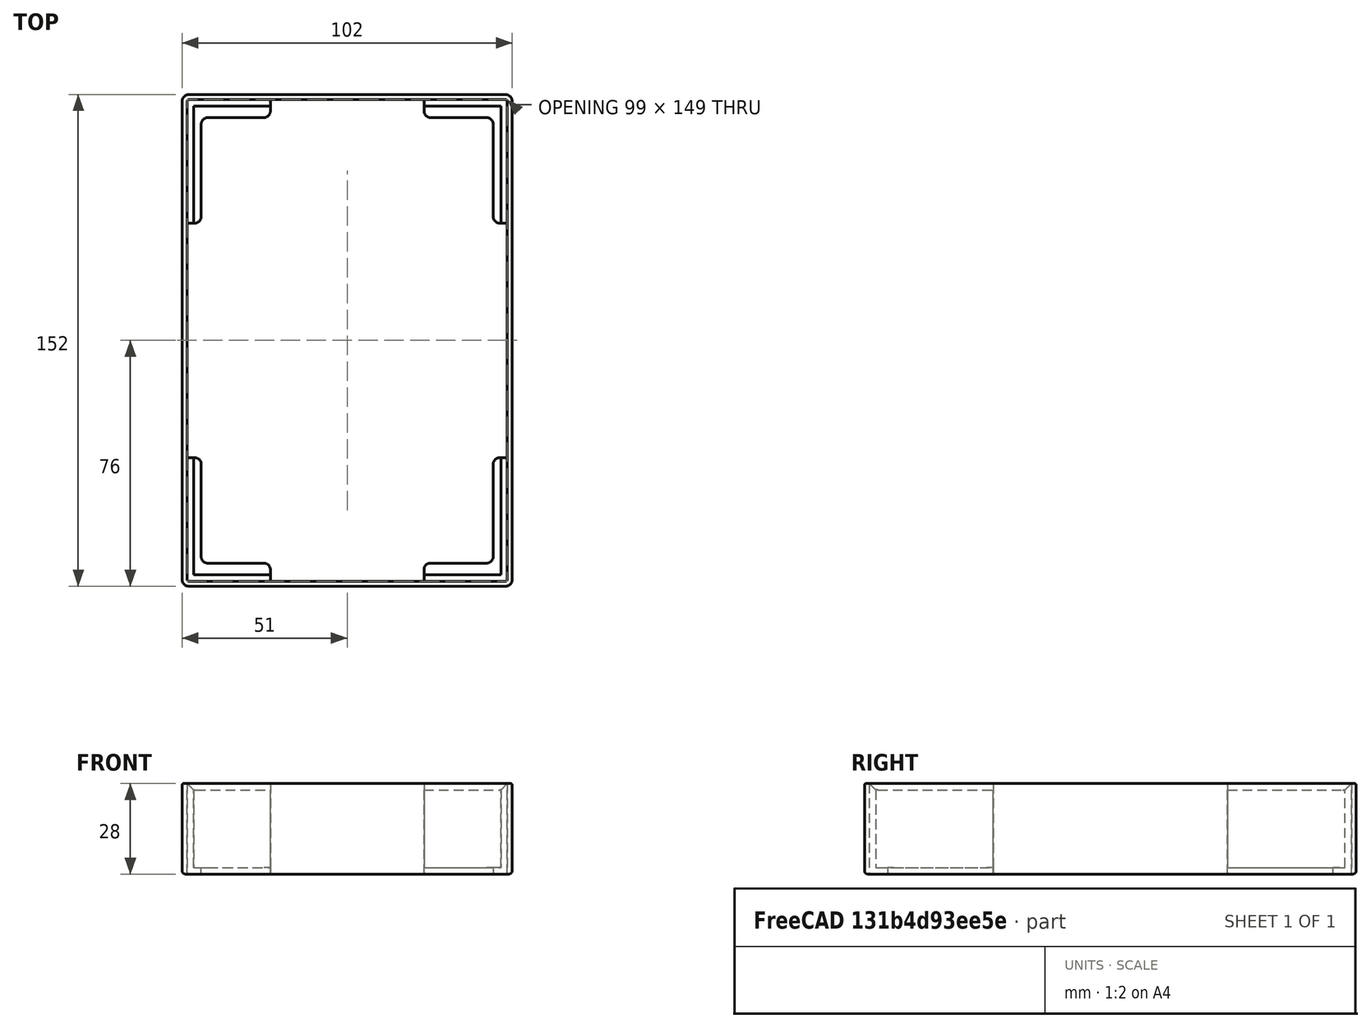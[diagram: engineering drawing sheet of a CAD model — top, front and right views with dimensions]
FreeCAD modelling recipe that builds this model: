
FCSTD DOCUMENT  (FreeCAD 1.0R39109 (Git))
Label: Hero Realms Lid Inset CAD
License: All rights reserved
LicenseURL: https://en.wikipedia.org/wiki/All_rights_reserved
objects: PartDesign::Fillet×5, Part::Feature×2, Mesh::Feature×1, Part::Refine×1, PartDesign::FeatureBase×1, PartDesign::Chamfer×1, PartDesign::Body×1
note: 24 computed .brp shape members not serialized (recipe doc carries the construction recipe); baked Part::Feature solids carry a one-line shape summary decoded from their .brp

FEATURE [Mesh::Feature] Hero_Realms_Lid_Inset  label="Hero Realms Lid Inset"
FEATURE [Part::Feature] Hero_Realms_Lid_Inset001
  shape: bbox 102 x 152 x 28 mm, 176 faces, 0 solids (baked)
FEATURE [Part::Feature] Hero_Realms_Lid_Inset001_solid  label="Hero_Realms_Lid_Inset001 (Solid)"
  shape: bbox 102 x 152 x 28 mm, 176 faces (baked)
FEATURE [Part::Refine] Hero_Realms_Lid_Inset001_solid001  label="Hero_Realms_Lid_Inset001 (Solid)001"
  Source = -> Hero_Realms_Lid_Inset001_solid
FEATURE [PartDesign::FeatureBase] BaseFeature
  BaseFeature = -> Hero_Realms_Lid_Inset001_solid001
  Suppressed = false
FEATURE [PartDesign::Fillet] Fillet
  Base = -> BaseFeature [Edge38,Edge4,Edge36,Edge2]
  BaseFeature = -> BaseFeature
  Radius = 2
  Refine = true
  SupportTransform = false
  Suppressed = false
  UseAllEdges = false
FEATURE [PartDesign::Fillet] Fillet001
  Base = -> Fillet [Edge11,Edge10,Edge8,Edge1,Edge6,Edge5,Edge7,Edge9]
  BaseFeature = -> Fillet
  Radius = 1
  Refine = true
  SupportTransform = false
  Suppressed = false
  UseAllEdges = false
FEATURE [PartDesign::Chamfer] Chamfer
  Angle = 45
  Base = -> Fillet001 [Edge23,Edge24,Edge30,Edge31,Edge37,Edge38,Edge44,Edge17]
  BaseFeature = -> Fillet001
  ChamferType = 0
  FlipDirection = false
  Refine = true
  Size = 2
  Size2 = 1
  SupportTransform = false
  Suppressed = false
  UseAllEdges = false
FEATURE [PartDesign::Fillet] Fillet002
  Base = -> Chamfer [Edge14,Edge16,Edge18,Edge20,Edge19,Edge17,Edge15,Edge13]
  BaseFeature = -> Chamfer
  Radius = 0.5
  Refine = true
  SupportTransform = false
  Suppressed = false
  UseAllEdges = false
FEATURE [PartDesign::Fillet] Fillet003
  Base = -> Fillet002 [Edge39,Edge59,Edge69,Edge49]
  BaseFeature = -> Fillet002
  Radius = 1
  Refine = true
  SupportTransform = false
  Suppressed = false
  UseAllEdges = false
FEATURE [PartDesign::Fillet] Fillet004
  Base = -> Fillet003 [Edge99,Edge187,Edge136,Vertex108,Vertex128,Edge203,Edge148,Vertex111,Edge157,Edge167,Edge199,Edge162,Edge140,Edge197,Edge152]
  BaseFeature = -> Fillet003
  Radius = 2
  Refine = true
  SupportTransform = false
  Suppressed = false
  UseAllEdges = false
FEATURE [PartDesign::Body] Body
  AllowCompound = false
  BaseFeature = -> Hero_Realms_Lid_Inset001_solid001
  Group = -> [BaseFeature,Fillet,Fillet001,Chamfer,Fillet002,Fillet003,Fillet004]
  Origin = -> Origin
  Tip = -> Fillet004
